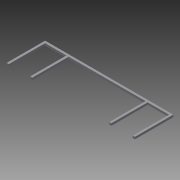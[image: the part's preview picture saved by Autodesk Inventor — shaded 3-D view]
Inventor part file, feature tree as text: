
AUTODESK INVENTOR PART (.ipt)
format: ipt  version: 2014 (Build 180170000, 170)  size: 97,792 bytes
history: native  units: in
note: dims shown in document units (in); Inventor stores cm internally (conversion verified against a paired STEP export)
features: extrude x3, sketch x3
ambient origin geometry x8: Origin, YZ Plane, XZ Plane, XY Plane, X Axis, Y Axis, Z Axis, Center Point
bodies: Solid1 (feature_tree)
feature tree (6):
  extrude  "Extrusion1"  Depth=36.0in
  extrude  "Extrusion2"  Depth=116.0in
  extrude  "Extrusion3"  Depth=2.0in TaperAngle=0.0deg
  sketch  "Sketch1"  dims[d0=120.0in d1=36.0in]
  sketch  "Sketch2"  dims[d2=2.0in d3=0.0in d4=116.0in]
  sketch  "Sketch3"  dims[d5=34.0in d6=17.4375in d7=0.0in d8=2.0in d9=2.0in d10=20.0in d11=20.0in d12=2.0in d13=0.0in]
